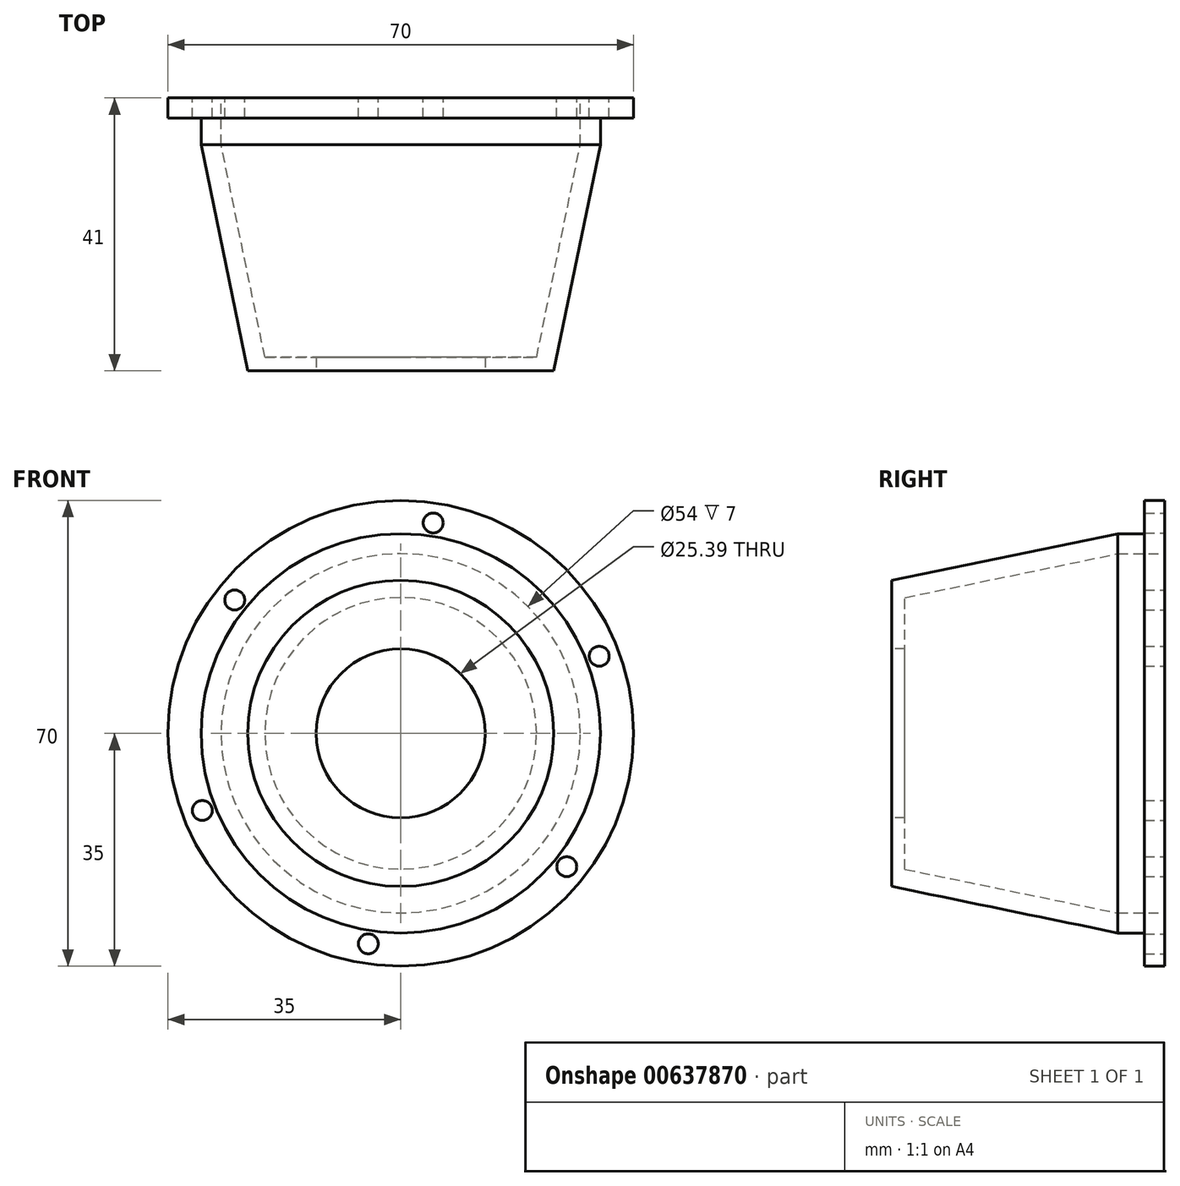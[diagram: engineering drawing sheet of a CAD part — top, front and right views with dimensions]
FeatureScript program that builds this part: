
annotation { "Feature Type Name" : "Feature", "Feature Type Description" : "" }
export const myFeature = defineFeature(function(context is Context, id is Id, definition is map)
    precondition{}
    {
        {
            var Q0;
            Q0=qCreatedBy(makeId("Front.planeOp"),FACE);
            var sketch = newSketch(context, id + "F0", { "sketchPlane" : qUnion([Q0])});
            skCircle(sketch, "E0", {"center": v(0, 0) * mm, "radius": 30 * mm});
            skCircle(sketch, "E1", {"center": v(0, 0) * mm, "radius": 27 * mm});
            skSolve(sketch);
        }
        {
            var Q0;
            Q0=qSketchRegion(id+"F0",true);
            extrude(context, id + "F1", {"entities" : qUnion([Q0]), "depth" : 4 * mm, "offsetDistance" : 25 * mm});
        }
        {
            var Q0;
            Q0=qCreatedBy(makeId("Front.planeOp"),FACE);
            cPlane(context, id + "F2", {"entities" : qUnion([Q0]), "cplaneType" : CPlaneType.OFFSET, "offset" : 38 * mm, "width" : 150 * mm, "height" : 150 * mm});
        }
        {
            var Q0;
            Q0=qCreatedBy(id+"F2.planeOp",FACE);
            var sketch = newSketch(context, id + "F3", { "sketchPlane" : qUnion([Q0])});
            skCircle(sketch, "E2", {"center": v(0, 0) * mm, "radius": 23 * mm});
            skCircle(sketch, "E3", {"center": v(0, 0) * mm, "radius": 20 * mm, "construction": true});
            skSolve(sketch);
        }
        {
            var Q0;
            Q0=makeQuery(id+"F1.opExtrude","CAP_FACE",FACE,{"disambiguationData":[OSD([sQuery(id+"F0.wireOp",EDGE,"E0"),sQuery(id+"F0.wireOp",EDGE,"E1")])],"isStart":false});
            var sketch = newSketch(context, id + "F4", { "sketchPlane" : qUnion([Q0])});
            skCircle(sketch, "E4", {"center": v(0, 0) * mm, "radius": 30 * mm});
            skCircle(sketch, "E5", {"center": v(0, 0) * mm, "radius": 27 * mm, "construction": true});
            skSolve(sketch);
        }
        {
            var Q1;
            Q1=qSketchRegion(id+"F4",true);
            var Q2;
            Q2=qSketchRegion(id+"F3",true);
            loft(context, id + "F5", {"operationType" : NewBodyOperationType.ADD, "sheetProfilesArray" : [{ "sheetProfileEntities" : qUnion([Q1]) }, { "sheetProfileEntities" : qUnion([Q2]) }]});
        }
        {
            var Q0;
            Q0=makeQuery(id+"F5.opLoft","CAP_FACE",FACE,{"disambiguationData":[OSD([makeQuery(id+"F4.imprint","IMPRINT",FACE,{"disambiguationData":[TD([[makeQuery(id+"F4.imprint","IMPRINT",EDGE,{"derivedFrom":makeQuery(id+"F1.opExtrude","CAP_EDGE",EDGE,{"disambiguationData":[OSD([sQuery(id+"F0.wireOp",EDGE,"E1")])],"isStart":false})}),1.0]])]})])],"isStart":true});
            var sketch = newSketch(context, id + "F6", { "sketchPlane" : qUnion([Q0])});
            skCircle(sketch, "E6", {"center": v(0, 0) * mm, "radius": 27 * mm});
            skSolve(sketch);
        }
        {
            var Q0;
            Q0=makeQuery(id+"F5.opLoft","CAP_FACE",FACE,{"disambiguationData":[OSD([makeQuery(id+"F3.imprint","IMPRINT",FACE,{"disambiguationData":[TD([[makeQuery(id+"F3.imprint","IMPRINT",EDGE,{"derivedFrom":sQuery(id+"F3.wireOp",EDGE,"E2")}),1.0]])]})])],"isStart":true});
            var sketch = newSketch(context, id + "F7", { "sketchPlane" : qUnion([Q0])});
            skCircle(sketch, "E7", {"center": v(0, 0) * mm, "radius": 20 * mm});
            skSolve(sketch);
        }
        {
            var Q1;
            Q1=qSketchRegion(id+"F7",true);
            var Q2;
            Q2=qSketchRegion(id+"F6",true);
            loft(context, id + "F8", {"operationType" : NewBodyOperationType.REMOVE, "sheetProfilesArray" : [{ "sheetProfileEntities" : qUnion([Q1]) }, { "sheetProfileEntities" : qUnion([Q2]) }]});
        }
        {
            var Q0;
            Q0=makeQuery(id+"F5.opLoft","CAP_FACE",FACE,{"disambiguationData":[OSD([makeQuery(id+"F3.imprint","IMPRINT",FACE,{"disambiguationData":[TD([[makeQuery(id+"F3.imprint","IMPRINT",EDGE,{"derivedFrom":sQuery(id+"F3.wireOp",EDGE,"E2")}),1.0]])]})])],"isStart":true});
            var sketch = newSketch(context, id + "F9", { "sketchPlane" : qUnion([Q0])});
            skCircle(sketch, "E8", {"center": v(0, 0) * mm, "radius": 22.4 * mm});
            skCircle(sketch, "E9", {"center": v(0, 0) * mm, "radius": 12.7 * mm});
            skSolve(sketch);
        }
        {
            var Q0;
            Q0=qSketchRegion(id+"F9",true);
            extrude(context, id + "F10", {"entities" : qUnion([Q0]), "operationType" : NewBodyOperationType.ADD, "oppositeDirection" : true, "depth" : 2 * mm, "offsetDistance" : 25 * mm});
        }
        {
            var Q0;
            Q0=makeQuery(id+"F1.opExtrude","CAP_FACE",FACE,{"disambiguationData":[OSD([sQuery(id+"F0.wireOp",EDGE,"E0"),sQuery(id+"F0.wireOp",EDGE,"E1")])],"isStart":true});
            var sketch = newSketch(context, id + "F11", { "sketchPlane" : qUnion([Q0])});
            skCircle(sketch, "E10", {"center": v(0, 0) * mm, "radius": 27 * mm});
            skCircle(sketch, "E11", {"center": v(0, 0) * mm, "radius": 35 * mm});
            skSolve(sketch);
        }
        {
            var Q0;
            Q0=qSketchRegion(id+"F11",true);
            extrude(context, id + "F12", {"entities" : qUnion([Q0]), "operationType" : NewBodyOperationType.ADD, "depth" : 3 * mm, "offsetDistance" : 25 * mm});
        }
        {
            var Q0;
            Q0=makeQuery(id+"F12.opExtrude","CAP_FACE",FACE,{"disambiguationData":[OSD([sQuery(id+"F11.wireOp",EDGE,"E10"),sQuery(id+"F11.wireOp",EDGE,"E11")])],"isStart":false});
            var sketch = newSketch(context, id + "F13", { "sketchPlane" : qUnion([Q0])});
            skCircle(sketch, "E12.cCircle", {"center": v(0, 0) * mm, "radius": 27.71 * mm, "construction": true});
            skLineSegment(sketch, "E12.0", {"start": v(-24.95, -20.04) * mm, "end": v(4.88, -31.63) * mm, "construction": true});
            skLineSegment(sketch, "E12.1", {"start": v(-29.83, 11.59) * mm, "end": v(-24.95, -20.04) * mm, "construction": true});
            skLineSegment(sketch, "E12.2", {"start": v(-4.88, 31.63) * mm, "end": v(-29.83, 11.59) * mm, "construction": true});
            skLineSegment(sketch, "E12.3", {"start": v(24.95, 20.04) * mm, "end": v(-4.88, 31.63) * mm, "construction": true});
            skLineSegment(sketch, "E12.4", {"start": v(29.83, -11.59) * mm, "end": v(24.95, 20.04) * mm, "construction": true});
            skLineSegment(sketch, "E12.5", {"start": v(4.88, -31.63) * mm, "end": v(29.83, -11.59) * mm, "construction": true});
            skPoint(sketch, "E12.0.midPoint", {"position": v(-10.04, -25.83) * mm});
            skCircle(sketch, "E13", {"center": v(-4.88, 31.63) * mm, "radius": 1.5 * mm});
            skCircle(sketch, "E14", {"center": v(24.95, 20.04) * mm, "radius": 1.5 * mm});
            skCircle(sketch, "E15", {"center": v(29.83, -11.59) * mm, "radius": 1.5 * mm});
            skCircle(sketch, "E16", {"center": v(4.88, -31.63) * mm, "radius": 1.5 * mm});
            skCircle(sketch, "E17", {"center": v(-24.95, -20.04) * mm, "radius": 1.5 * mm});
            skCircle(sketch, "E18", {"center": v(-29.83, 11.59) * mm, "radius": 1.5 * mm});
            skSolve(sketch);
        }
        {
            var Q0;
            Q0=qSketchRegion(id+"F13",true);
            extrude(context, id + "F14", {"entities" : qUnion([Q0]), "operationType" : NewBodyOperationType.REMOVE, "oppositeDirection" : true, "depth" : 25 * mm, "offsetDistance" : 25 * mm});
        }
    });
